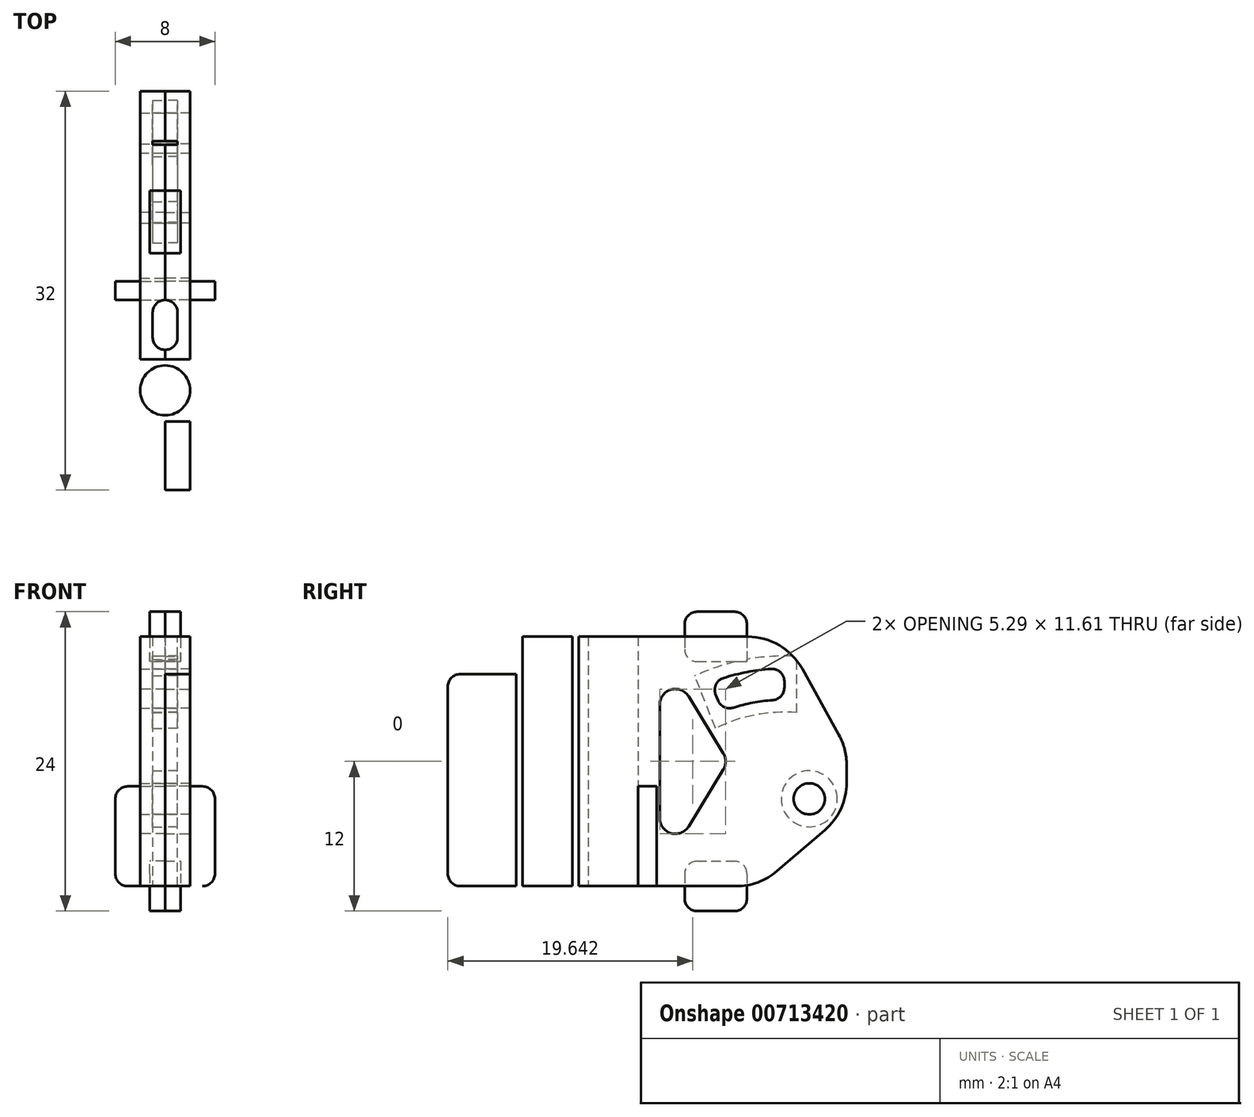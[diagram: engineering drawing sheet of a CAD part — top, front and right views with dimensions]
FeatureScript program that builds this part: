
annotation { "Feature Type Name" : "Feature", "Feature Type Description" : "" }
export const myFeature = defineFeature(function(context is Context, id is Id, definition is map)
    precondition{}
    {
        {
            var Q0;
            Q0=qCreatedBy(makeId("Right.planeOp"),FACE);
            var sketch = newSketch(context, id + "F0", { "sketchPlane" : qUnion([Q0])});
            skLineSegment(sketch, "E0.bottom", {"start": v(2.5, 0) * mm, "end": v(7, 0) * mm});
            skLineSegment(sketch, "E0.top", {"start": v(2.5, 20) * mm, "end": v(7, 20) * mm});
            skLineSegment(sketch, "E0.left", {"start": v(2.5, 0) * mm, "end": v(2.5, 20) * mm});
            skLineSegment(sketch, "E0.right", {"start": v(7, 0) * mm, "end": v(7, 20) * mm});
            skLineSegment(sketch, "E1", {"start": v(17, 0) * mm, "end": v(7, 0) * mm});
            skLineSegment(sketch, "E2", {"start": v(17, 0) * mm, "end": v(24, 6) * mm});
            skLineSegment(sketch, "E3", {"start": v(19, 20) * mm, "end": v(7, 20) * mm});
            skLineSegment(sketch, "E4", {"start": v(24, 6) * mm, "end": v(24, 11) * mm});
            skLineSegment(sketch, "E5", {"start": v(24, 11) * mm, "end": v(19, 20) * mm});
            skLineSegment(sketch, "E6", {"start": v(9, 19) * mm, "end": v(9, 1) * mm});
            skLineSegment(sketch, "E7", {"start": v(9, 1) * mm, "end": v(14.5, 10) * mm});
            skLineSegment(sketch, "E8", {"start": v(14.5, 10) * mm, "end": v(9, 19) * mm});
            skCircle(sketch, "E9", {"center": v(21, 7) * mm, "radius": 1.25 * mm});
            skArc(sketch, "E10", {"start": v(19, 17.45) * mm, "mid": v(16, 17.17) * mm, "end": v(13.1, 16.32) * mm});
            skArc(sketch, "E11", {"start": v(19, 14.95) * mm, "mid": v(16.47, 14.7) * mm, "end": v(14.03, 14) * mm});
            skLineSegment(sketch, "E12", {"start": v(19, 14.95) * mm, "end": v(19, 17.45) * mm});
            skLineSegment(sketch, "E13", {"start": v(14.03, 14) * mm, "end": v(13.1, 16.32) * mm});
            skLineSegment(sketch, "E14", {"start": v(9, 19) * mm, "end": v(9, 20) * mm, "construction": true});
            skLineSegment(sketch, "E15", {"start": v(9, 1) * mm, "end": v(9, 0) * mm, "construction": true});
            skLineSegment(sketch, "E16.bottom", {"start": v(-2.5, 0) * mm, "end": v(-8, 0) * mm});
            skLineSegment(sketch, "E16.top", {"start": v(-2.5, 17) * mm, "end": v(-8, 17) * mm});
            skLineSegment(sketch, "E16.left", {"start": v(-2.5, 0) * mm, "end": v(-2.5, 17) * mm});
            skLineSegment(sketch, "E16.right", {"start": v(-8, 0) * mm, "end": v(-8, 17) * mm});
            skLineSegment(sketch, "E17", {"start": v(-2.5, 0) * mm, "end": v(0, 0) * mm, "construction": true});
            skLineSegment(sketch, "E18", {"start": v(0, 0) * mm, "end": v(2.5, 0) * mm, "construction": true});
            skCircle(sketch, "E19.0", {"center": v(21, 7) * mm, "radius": 2.25 * mm});
            skArc(sketch, "E20.0", {"start": v(20, 18.42) * mm, "mid": v(15.81, 18.15) * mm, "end": v(11.82, 16.86) * mm});
            skLineSegment(sketch, "E20.1", {"start": v(20, 13.9) * mm, "end": v(20, 18.42) * mm});
            skArc(sketch, "E20.2", {"start": v(20, 13.9) * mm, "mid": v(16.66, 13.73) * mm, "end": v(13.48, 12.66) * mm});
            skLineSegment(sketch, "E20.3", {"start": v(13.48, 12.66) * mm, "end": v(11.82, 16.86) * mm});
            skSolve(sketch);
        }
        {
            var Q0;
            Q0=makeQuery(id+"F0.imprint","IMPRINT",FACE,{"disambiguationData":[TD([[makeQuery(id+"F0.imprint","IMPRINT",EDGE,{"derivedFrom":sQuery(id+"F0.wireOp",EDGE,"E0.right")}),-1.0]])]});
            var Q1;
            Q1=makeQuery(id+"F0.imprint","IMPRINT",FACE,{"disambiguationData":[TD([[makeQuery(id+"F0.imprint","IMPRINT",EDGE,{"derivedFrom":sQuery(id+"F0.wireOp",EDGE,"E0.bottom")}),1.0]])]});
            var Q2;
            Q2=makeQuery(id+"F0.imprint","IMPRINT",FACE,{"disambiguationData":[TD([[makeQuery(id+"F0.imprint","IMPRINT",EDGE,{"derivedFrom":sQuery(id+"F0.wireOp",EDGE,"xB6x6uVb-zKhv-ANQq-UcW5-hUPj4CPM5JXQ.bottom")}),-1.0]])]});
            var Q3;
            Q3=makeQuery(id+"F0.imprint","IMPRINT",FACE,{"disambiguationData":[TD([[makeQuery(id+"F0.imprint","IMPRINT",EDGE,{"derivedFrom":sQuery(id+"F0.wireOp",EDGE,"IHIChXXd-N6sl-k9xa-xTSY-nWWbFs0pZ4qy.bottom")}),1.0]])]});
            var Q4;
            Q4=makeQuery(id+"F0.imprint","IMPRINT",FACE,{"disambiguationData":[TD([[makeQuery(id+"F0.imprint","IMPRINT",EDGE,{"derivedFrom":sQuery(id+"F0.wireOp",EDGE,"36cd0414-5def-4b73-8972-37efab1353b10.MirrorCS")}),1.0]])]});
            var Q5;
            Q5=makeQuery(id+"F0.imprint","IMPRINT",FACE,{"disambiguationData":[TD([[makeQuery(id+"F0.imprint","IMPRINT",EDGE,{"derivedFrom":sQuery(id+"F0.wireOp",EDGE,"E16.bottom")}),-1.0]])]});
            var Q6;
            Q6=makeQuery(id+"F0.imprint","IMPRINT",FACE,{"disambiguationData":[TD([[makeQuery(id+"F0.imprint","IMPRINT",EDGE,{"derivedFrom":sQuery(id+"F0.wireOp",EDGE,"E10")}),-1.0]])]});
            var Q7;
            Q7=makeQuery(id+"F0.imprint","IMPRINT",FACE,{"disambiguationData":[TD([[makeQuery(id+"F0.imprint","IMPRINT",EDGE,{"derivedFrom":sQuery(id+"F0.wireOp",EDGE,"E9")}),-1.0]])]});
            extrude(context, id + "F1", {"entities" : qUnion([Q0, Q1, Q2, Q3, Q4, Q5, Q6, Q7]), "depth" : 2 * mm, "offsetDistance" : 25 * mm});
        }
        {
            var Q0;
            Q0=qCreatedBy(makeId("Top.planeOp"),FACE);
            var sketch = newSketch(context, id + "F2", { "sketchPlane" : qUnion([Q0])});
            skCircle(sketch, "E21.MirrorC", {"center": v(0, 0) * mm, "radius": 3.25 * mm});
            skCircle(sketch, "E22.MirrorC", {"center": v(0, 0) * mm, "radius": 2 * mm});
            skLineSegment(sketch, "E23.MirrorCS", {"start": v(-4, 8.75) * mm, "end": v(-4, 7.25) * mm});
            skLineSegment(sketch, "E24.MirrorCS", {"start": v(-4, 7.25) * mm, "end": v(0, 7.25) * mm});
            skLineSegment(sketch, "E25", {"start": v(0, 7.25) * mm, "end": v(0, 8.75) * mm});
            skLineSegment(sketch, "E26", {"start": v(-4, 8.75) * mm, "end": v(0, 8.75) * mm});
            skLineSegment(sketch, "E27.bottom", {"start": v(0, 11) * mm, "end": v(-1.25, 11) * mm});
            skLineSegment(sketch, "E27.top", {"start": v(0, 16) * mm, "end": v(-1.25, 16) * mm});
            skLineSegment(sketch, "E27.left", {"start": v(0, 11) * mm, "end": v(0, 16) * mm});
            skLineSegment(sketch, "E27.right", {"start": v(-1.25, 11) * mm, "end": v(-1.25, 16) * mm});
            skLineSegment(sketch, "E28.bottom", {"start": v(0, 7.25) * mm, "end": v(1, 7.25) * mm});
            skLineSegment(sketch, "E28.top", {"start": v(0, 3.1) * mm, "end": v(1, 3.1) * mm});
            skLineSegment(sketch, "E28.left", {"start": v(0, 7.25) * mm, "end": v(0, 3.1) * mm});
            skLineSegment(sketch, "E28.right", {"start": v(1, 7.25) * mm, "end": v(1, 3.1) * mm});
            skSolve(sketch);
        }
        {
            var Q0;
            Q0=makeQuery(id+"F2.imprint","IMPRINT",FACE,{"disambiguationData":[TD([[makeQuery(id+"F2.imprint","IMPRINT",EDGE,{"derivedFrom":sQuery(id+"F2.wireOp",EDGE,"E22.MirrorC")}),1.0]])]});
            var Q1;
            {var subQ2=sQuery(id+"F2.wireOp",EDGE,"d09804f8-7da6-46d8-8f41-128a26d8790d1.MirrorCS");Q1=makeQuery(id+"F2.imprint","IMPRINT",FACE,{"disambiguationData":[TD([[makeQuery(id+"F2.imprint","IMPRINT",EDGE,{"derivedFrom":subQ2}),1.0]])]});}
            extrude(context, id + "F3", {"entities" : qUnion([Q0, Q1]), "operationType" : NewBodyOperationType.ADD, "depth" : 20 * mm, "offsetDistance" : 25 * mm});
        }
        {
            var Q0;
            Q0=makeQuery(id+"F2.imprint","IMPRINT",FACE,{"disambiguationData":[TD([[makeQuery(id+"F2.imprint","IMPRINT",EDGE,{"derivedFrom":sQuery(id+"F2.wireOp",EDGE,"E23.MirrorCS")}),1.0]])]});
            extrude(context, id + "F4", {"entities" : qUnion([Q0]), "operationType" : NewBodyOperationType.ADD, "depth" : 8 * mm, "offsetDistance" : 25 * mm});
        }
        {
            var Q0;
            Q0=makeQuery(id+"F2.imprint","IMPRINT",FACE,{"disambiguationData":[TD([[makeQuery(id+"F2.imprint","IMPRINT",EDGE,{"derivedFrom":sQuery(id+"F2.wireOp",EDGE,"E27.bottom")}),-1.0]])]});
            extrude(context, id + "F5", {"entities" : qUnion([Q0]), "operationType" : NewBodyOperationType.ADD, "depth" : 2 * mm, "offsetDistance" : 25 * mm, "hasSecondDirection" : true, "secondDirectionOppositeDirection" : true, "secondDirectionDepth" : 2 * mm});
        }
        {
            var Q0;
            Q0=makeQuery(id+"F2.imprint","IMPRINT",FACE,{"disambiguationData":[TD([[makeQuery(id+"F2.imprint","IMPRINT",EDGE,{"derivedFrom":sQuery(id+"F2.wireOp",EDGE,"E27.bottom")}),-1.0]])]});
            extrude(context, id + "F6", {"entities" : qUnion([Q0]), "operationType" : NewBodyOperationType.ADD, "depth" : 22 * mm, "offsetDistance" : 25 * mm, "hasSecondDirection" : true, "secondDirectionOppositeDirection" : false, "secondDirectionDepth" : 18 * mm});
        }
        {
            var Q0;
            {var subQ4=sQuery(id+"F2.wireOp",EDGE,"E28.bottom");Q0=makeQuery(id+"F2.imprint","IMPRINT",FACE,{"disambiguationData":[TD([[makeQuery(id+"F2.imprint","IMPRINT",EDGE,{"derivedFrom":subQ4}),-1.0]])]});}
            extrude(context, id + "F7", {"entities" : qUnion([Q0]), "operationType" : NewBodyOperationType.REMOVE, "endBound" : BoundingType.THROUGH_ALL, "depth" : 25 * mm, "offsetDistance" : 25 * mm});
        }
        {
            var Q0;
            Q0=makeQuery(id+"F0.imprint","IMPRINT",FACE,{"disambiguationData":[TD([[makeQuery(id+"F0.imprint","IMPRINT",EDGE,{"derivedFrom":sQuery(id+"F0.wireOp",EDGE,"E9")}),-1.0]])]});
            var Q1;
            Q1=makeQuery(id+"F0.imprint","IMPRINT",FACE,{"disambiguationData":[TD([[makeQuery(id+"F0.imprint","IMPRINT",EDGE,{"derivedFrom":sQuery(id+"F0.wireOp",EDGE,"E10")}),-1.0]])]});
            extrude(context, id + "F8", {"entities" : qUnion([Q0, Q1]), "operationType" : NewBodyOperationType.ADD, "oppositeDirection" : true, "depth" : 1 * mm, "offsetDistance" : 25 * mm});
        }
        {
            var Q0;
            Q0=makeQuery(id+"F1.opExtrude","SWEPT_EDGE",EDGE,{"disambiguationData":[OSD([sQuery(id+"F0.wireOp",EDGE,"xB6x6uVb-zKhv-ANQq-UcW5-hUPj4CPM5JXQ.top"),sQuery(id+"F0.wireOp",EDGE,"xB6x6uVb-zKhv-ANQq-UcW5-hUPj4CPM5JXQ.left")])]});
            var Q1;
            Q1=makeQuery(id+"F1.opExtrude","SWEPT_EDGE",EDGE,{"disambiguationData":[OSD([sQuery(id+"F0.wireOp",EDGE,"xB6x6uVb-zKhv-ANQq-UcW5-hUPj4CPM5JXQ.top"),sQuery(id+"F0.wireOp",EDGE,"xB6x6uVb-zKhv-ANQq-UcW5-hUPj4CPM5JXQ.right")])]});
            var Q2;
            Q2=makeQuery(id+"F4.opExtrude","CAP_EDGE",EDGE,{"disambiguationData":[OSD([sQuery(id+"F2.wireOp",EDGE,"E23.MirrorCS")])],"isStart":false});
            var Q3;
            Q3=makeQuery(id+"F4.opExtrude","CAP_EDGE",EDGE,{"disambiguationData":[OSD([sQuery(id+"F2.wireOp",EDGE,"E23.MirrorCS")])],"isStart":true});
            var Q4;
            Q4=makeQuery(id+"F1.opExtrude","SWEPT_EDGE",EDGE,{"disambiguationData":[OSD([sQuery(id+"F0.wireOp",EDGE,"E11"),sQuery(id+"F0.wireOp",EDGE,"E13")])]});
            var Q5;
            Q5=makeQuery(id+"F1.opExtrude","SWEPT_EDGE",EDGE,{"disambiguationData":[OSD([sQuery(id+"F0.wireOp",EDGE,"E10"),sQuery(id+"F0.wireOp",EDGE,"E13")])]});
            var Q6;
            Q6=makeQuery(id+"F1.opExtrude","SWEPT_EDGE",EDGE,{"disambiguationData":[OSD([sQuery(id+"F0.wireOp",EDGE,"E10"),sQuery(id+"F0.wireOp",EDGE,"E12")])]});
            var Q7;
            Q7=makeQuery(id+"F1.opExtrude","SWEPT_EDGE",EDGE,{"disambiguationData":[OSD([sQuery(id+"F0.wireOp",EDGE,"E11"),sQuery(id+"F0.wireOp",EDGE,"E12")])]});
            var Q8;
            Q8=makeQuery(id+"F5.opExtrude","CAP_EDGE",EDGE,{"disambiguationData":[OSD([sQuery(id+"F2.wireOp",EDGE,"E27.left")])],"isStart":false});
            var Q9;
            Q9=makeQuery(id+"F5.opExtrude","CAP_EDGE",EDGE,{"disambiguationData":[OSD([sQuery(id+"F2.wireOp",EDGE,"E27.bottom")])],"isStart":false});
            var Q10;
            Q10=makeQuery(id+"F5.opExtrude","CAP_EDGE",EDGE,{"disambiguationData":[OSD([sQuery(id+"F2.wireOp",EDGE,"E27.top")])],"isStart":false});
            var Q11;
            Q11=makeQuery(id+"F5.opExtrude","CAP_EDGE",EDGE,{"disambiguationData":[OSD([sQuery(id+"F2.wireOp",EDGE,"E27.bottom")])],"isStart":true});
            var Q12;
            Q12=makeQuery(id+"F5.opExtrude","CAP_EDGE",EDGE,{"disambiguationData":[OSD([sQuery(id+"F2.wireOp",EDGE,"E27.top")])],"isStart":true});
            var Q13;
            Q13=makeQuery(id+"F6.opExtrude","CAP_EDGE",EDGE,{"disambiguationData":[OSD([sQuery(id+"F2.wireOp",EDGE,"E27.left")])],"isStart":true});
            var Q14;
            Q14=makeQuery(id+"F6.opExtrude","CAP_EDGE",EDGE,{"disambiguationData":[OSD([sQuery(id+"F2.wireOp",EDGE,"E27.bottom")])],"isStart":true});
            var Q15;
            Q15=makeQuery(id+"F6.opExtrude","CAP_EDGE",EDGE,{"disambiguationData":[OSD([sQuery(id+"F2.wireOp",EDGE,"E27.bottom")])],"isStart":false});
            var Q16;
            Q16=makeQuery(id+"F6.opExtrude","CAP_EDGE",EDGE,{"disambiguationData":[OSD([sQuery(id+"F2.wireOp",EDGE,"E27.top")])],"isStart":false});
            var Q17;
            Q17=makeQuery(id+"F7.boolean.opBoolean","COPY",EDGE,{"derivedFrom":makeQuery(id+"F7.opExtrude","SWEPT_EDGE",EDGE,{"disambiguationData":[OSD([sQuery(id+"F2.wireOp",EDGE,"E28.bottom"),sQuery(id+"F2.wireOp",EDGE,"E28.right")])]})});
            var Q18;
            Q18=makeQuery(id+"F7.boolean.opBoolean","COPY",EDGE,{"derivedFrom":makeQuery(id+"F7.opExtrude","SWEPT_EDGE",EDGE,{"disambiguationData":[OSD([sQuery(id+"F2.wireOp",EDGE,"E21.MirrorC"),sQuery(id+"F2.wireOp",EDGE,"E28.top"),sQuery(id+"F2.wireOp",EDGE,"E28.right")])]})});
            var Q19;
            Q19=makeQuery(id+"F1.opExtrude","SWEPT_EDGE",EDGE,{"disambiguationData":[OSD([sQuery(id+"F0.wireOp",EDGE,"60648e58-3a74-42ae-930e-64627e0052f30.MirrorCS"),sQuery(id+"F0.wireOp",EDGE,"cbf5a70c-ffd6-49c6-911a-603cd1f403520.MirrorCS")])]});
            var Q20;
            Q20=makeQuery(id+"F1.opExtrude","SWEPT_EDGE",EDGE,{"disambiguationData":[OSD([sQuery(id+"F0.wireOp",EDGE,"cbf5a70c-ffd6-49c6-911a-603cd1f403520.MirrorCS"),sQuery(id+"F0.wireOp",EDGE,"4e2fa409-8d6d-4920-9970-75c7dc6de36d0.MirrorCS")])]});
            var Q21;
            {var subQ0=sQuery(id+"F0.wireOp",EDGE,"E5");var subQ1=sQuery(id+"F0.wireOp",EDGE,"E20.0");Q21=makeQuery(id+"F8.boolean.opBoolean","SPLIT",EDGE,{"disambiguationData":[TD([makeQuery(id+"F1.opExtrude","SWEPT_FACE",FACE,{"disambiguationData":[OSD([subQ0])]})])],"derivedFrom":makeQuery(id+"F8.opExtrude","CAP_EDGE",EDGE,{"disambiguationData":[OSD([subQ1])],"isStart":true})});}
            var Q22;
            Q22=makeQuery(id+"F8.opExtrude","CAP_EDGE",EDGE,{"disambiguationData":[OSD([sQuery(id+"F0.wireOp",EDGE,"E19.0")])],"isStart":true});
            var Q23;
            Q23=makeQuery(id+"F1.opExtrude","SWEPT_EDGE",EDGE,{"disambiguationData":[OSD([sQuery(id+"F0.wireOp",EDGE,"E16.bottom"),sQuery(id+"F0.wireOp",EDGE,"E16.right")])]});
            var Q24;
            Q24=makeQuery(id+"F1.opExtrude","SWEPT_EDGE",EDGE,{"disambiguationData":[OSD([sQuery(id+"F0.wireOp",EDGE,"E16.top"),sQuery(id+"F0.wireOp",EDGE,"E16.right")])]});
            var Q25;
            Q25=makeQuery(id+"F8.opExtrude","CAP_EDGE",EDGE,{"disambiguationData":[OSD([sQuery(id+"F0.wireOp",EDGE,"E20.3")])],"isStart":true});
            var Q26;
            Q26=makeQuery(id+"F8.opExtrude","CAP_EDGE",EDGE,{"disambiguationData":[OSD([sQuery(id+"F0.wireOp",EDGE,"E20.2")])],"isStart":true});
            var Q27;
            Q27=makeQuery(id+"F8.opExtrude","CAP_EDGE",EDGE,{"disambiguationData":[OSD([sQuery(id+"F0.wireOp",EDGE,"E20.1")])],"isStart":true});
            fillet(context, id + "F9", {"entities" : qUnion([Q0, Q1, Q2, Q3, Q4, Q5, Q6, Q7, Q8, Q9, Q10, Q11, Q12, Q13, Q14, Q15, Q16, Q17, Q18, Q19, Q20, Q21, Q22, Q23, Q24, Q25, Q26, Q27]), "radius" : 1 * mm, "tangentPropagation" : true, "allowEdgeOverflow" : false});
        }
        {
            var Q0;
            Q0=makeQuery(id+"F1.opExtrude","SWEPT_EDGE",EDGE,{"disambiguationData":[OSD([sQuery(id+"F0.wireOp",EDGE,"E6"),sQuery(id+"F0.wireOp",EDGE,"E8")])]});
            var Q1;
            Q1=makeQuery(id+"F1.opExtrude","SWEPT_EDGE",EDGE,{"disambiguationData":[OSD([sQuery(id+"F0.wireOp",EDGE,"E7"),sQuery(id+"F0.wireOp",EDGE,"E8")])]});
            var Q2;
            Q2=makeQuery(id+"F1.opExtrude","SWEPT_EDGE",EDGE,{"disambiguationData":[OSD([sQuery(id+"F0.wireOp",EDGE,"E6"),sQuery(id+"F0.wireOp",EDGE,"E7")])]});
            fillet(context, id + "F10", {"entities" : qUnion([Q0, Q1, Q2]), "radius" : 1.25 * mm, "tangentPropagation" : true, "allowEdgeOverflow" : false});
        }
        {
            var Q0;
            Q0=makeQuery(id+"F3.boolean.opBoolean","INTERSECT",EDGE,{"derivedFrom":[makeQuery(id+"F1.opExtrude","CAP_FACE",FACE,{"disambiguationData":[OSD([sQuery(id+"F0.wireOp",EDGE,"E0.bottom"),sQuery(id+"F0.wireOp",EDGE,"E0.top"),sQuery(id+"F0.wireOp",EDGE,"E0.left"),sQuery(id+"F0.wireOp",EDGE,"E1"),sQuery(id+"F0.wireOp",EDGE,"E2"),sQuery(id+"F0.wireOp",EDGE,"E3"),sQuery(id+"F0.wireOp",EDGE,"E4"),sQuery(id+"F0.wireOp",EDGE,"E5"),sQuery(id+"F0.wireOp",EDGE,"E6"),sQuery(id+"F0.wireOp",EDGE,"E7"),sQuery(id+"F0.wireOp",EDGE,"E8"),sQuery(id+"F0.wireOp",EDGE,"E9"),sQuery(id+"F0.wireOp",EDGE,"E10"),sQuery(id+"F0.wireOp",EDGE,"E11"),sQuery(id+"F0.wireOp",EDGE,"E12"),sQuery(id+"F0.wireOp",EDGE,"E13")])],"isStart":false}),makeQuery(id+"F3.opExtrude","SWEPT_FACE",FACE,{"disambiguationData":[OSD([sQuery(id+"F2.wireOp",EDGE,"E21.MirrorC")])]})]});
            var Q1;
            Q1=makeQuery(id+"F3.boolean.opBoolean","INTERSECT",EDGE,{"derivedFrom":[makeQuery(id+"F1.opExtrude","CAP_FACE",FACE,{"disambiguationData":[OSD([sQuery(id+"F0.wireOp",EDGE,"E16.bottom"),sQuery(id+"F0.wireOp",EDGE,"E16.top"),sQuery(id+"F0.wireOp",EDGE,"E16.left"),sQuery(id+"F0.wireOp",EDGE,"E16.right")])],"isStart":true}),makeQuery(id+"F3.opExtrude","SWEPT_FACE",FACE,{"disambiguationData":[OSD([sQuery(id+"F2.wireOp",EDGE,"E21.MirrorC")])]})]});
            var Q2;
            Q2=makeQuery(id+"F3.boolean.opBoolean","INTERSECT",EDGE,{"derivedFrom":[makeQuery(id+"F1.opExtrude","CAP_FACE",FACE,{"disambiguationData":[OSD([sQuery(id+"F0.wireOp",EDGE,"E16.bottom"),sQuery(id+"F0.wireOp",EDGE,"E16.top"),sQuery(id+"F0.wireOp",EDGE,"E16.left"),sQuery(id+"F0.wireOp",EDGE,"E16.right")])],"isStart":false}),makeQuery(id+"F3.opExtrude","SWEPT_FACE",FACE,{"disambiguationData":[OSD([sQuery(id+"F2.wireOp",EDGE,"E21.MirrorC")])]})]});
            var Q3;
            Q3=makeQuery(id+"F1.opExtrude","SWEPT_EDGE",EDGE,{"disambiguationData":[OSD([sQuery(id+"F0.wireOp",EDGE,"E3"),sQuery(id+"F0.wireOp",EDGE,"E5")])]});
            var Q4;
            Q4=makeQuery(id+"F1.opExtrude","SWEPT_EDGE",EDGE,{"disambiguationData":[OSD([sQuery(id+"F0.wireOp",EDGE,"E4"),sQuery(id+"F0.wireOp",EDGE,"E5")])]});
            var Q5;
            Q5=makeQuery(id+"F1.opExtrude","SWEPT_EDGE",EDGE,{"disambiguationData":[OSD([sQuery(id+"F0.wireOp",EDGE,"E2"),sQuery(id+"F0.wireOp",EDGE,"E4")])]});
            var Q6;
            Q6=makeQuery(id+"F1.opExtrude","SWEPT_EDGE",EDGE,{"disambiguationData":[OSD([sQuery(id+"F0.wireOp",EDGE,"E1"),sQuery(id+"F0.wireOp",EDGE,"E2")])]});
            fillet(context, id + "F11", {"entities" : qUnion([Q0, Q1, Q2, Q3, Q4, Q5, Q6]), "radius" : 5 * mm, "tangentPropagation" : true, "allowEdgeOverflow" : false});
        }
        {
            var Q0;
            Q0=makeQuery(id+"F1.opExtrude","SWEPT_BODY",BODY,{"disambiguationData":[OSD([sQuery(id+"F0.wireOp",EDGE,"E0.bottom"),sQuery(id+"F0.wireOp",EDGE,"E0.top"),sQuery(id+"F0.wireOp",EDGE,"E0.left"),sQuery(id+"F0.wireOp",EDGE,"E1"),sQuery(id+"F0.wireOp",EDGE,"E2"),sQuery(id+"F0.wireOp",EDGE,"E3"),sQuery(id+"F0.wireOp",EDGE,"E4"),sQuery(id+"F0.wireOp",EDGE,"E5"),sQuery(id+"F0.wireOp",EDGE,"E6"),sQuery(id+"F0.wireOp",EDGE,"E7"),sQuery(id+"F0.wireOp",EDGE,"E8"),sQuery(id+"F0.wireOp",EDGE,"E9"),sQuery(id+"F0.wireOp",EDGE,"E10"),sQuery(id+"F0.wireOp",EDGE,"E11"),sQuery(id+"F0.wireOp",EDGE,"E12"),sQuery(id+"F0.wireOp",EDGE,"E13")])]});
            var Q1;
            Q1=qCreatedBy(makeId("Right.planeOp"),FACE);
            mirror(context, id + "F12", {"entities" : qUnion([Q0]), "mirrorPlane" : qUnion([Q1])});
        }
    });
